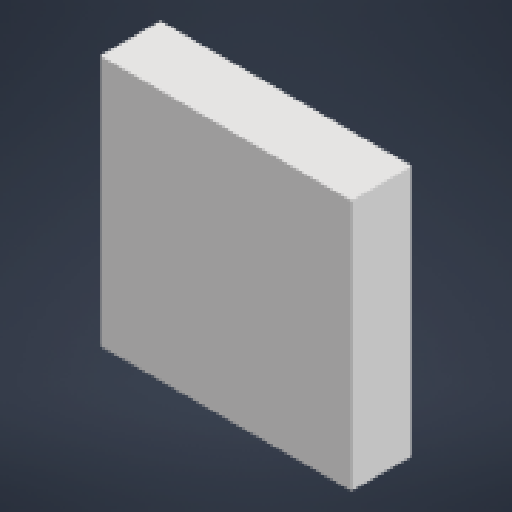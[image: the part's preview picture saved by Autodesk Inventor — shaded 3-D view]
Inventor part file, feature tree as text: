
AUTODESK INVENTOR PART (.ipt)
format: ipt  version: 2024 (Build 280153000, 153)  size: 115,712 bytes
history: native  units: mm
features: other x4, extrude x2, sketch x2, reference x2
ambient origin geometry x8: Origin, YZ Plane, XZ Plane, XY Plane, X Axis, Y Axis, Z Axis, Center Point
bodies: Body1 (feature_tree)
feature tree (10):
  other  "솔리드1"
  extrude  "돌출1"  Depth=2.0mm
  extrude  "돌출2"  Depth=5.0mm TaperAngle=0.0deg
  sketch  "스케치1"
  reference  "참조1"
  sketch  "스케치2"
  reference  "참조2"
  other  "<userpath>\Downloads\AAST\PART\AAST Remote Controler\apple logo light module.iam"
  other  "apple logo light module.iam"
  other  "light balance panel:1"
